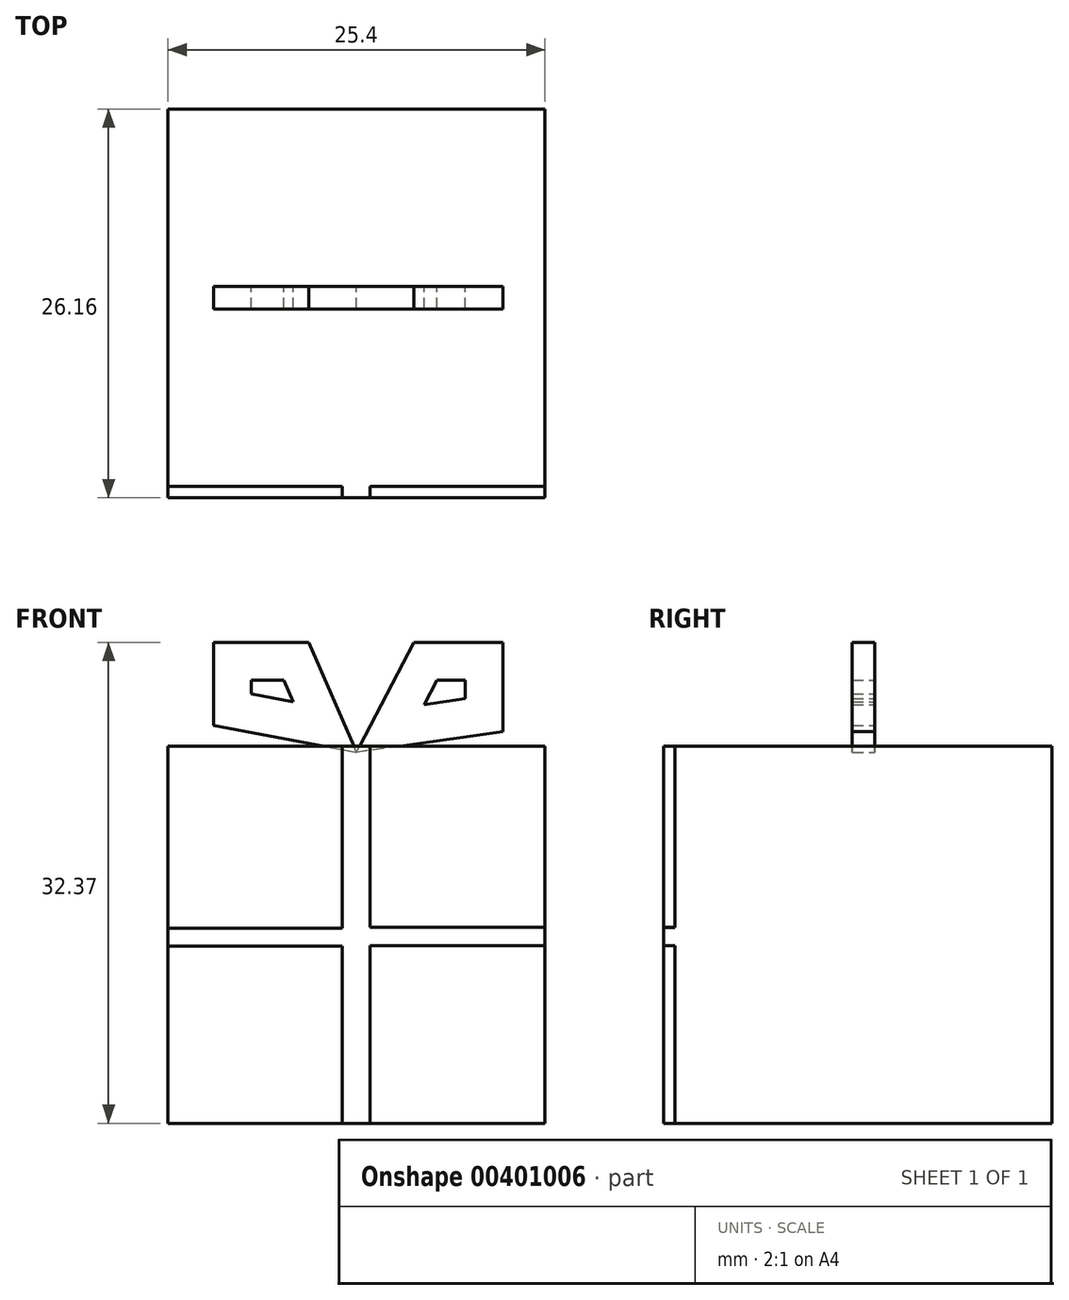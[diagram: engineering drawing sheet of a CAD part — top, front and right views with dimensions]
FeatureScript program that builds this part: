
annotation { "Feature Type Name" : "Feature", "Feature Type Description" : "" }
export const myFeature = defineFeature(function(context is Context, id is Id, definition is map)
    precondition{}
    {
        {
            var Q0;
            Q0=qCreatedBy(makeId("Right.planeOp"),FACE);
            var sketch = newSketch(context, id + "F0", { "sketchPlane" : qUnion([Q0])});
            skLineSegment(sketch, "E0.bottom", {"start": v(12.7, -12.7) * mm, "end": v(-12.7, -12.7) * mm});
            skLineSegment(sketch, "E0.top", {"start": v(12.7, 12.7) * mm, "end": v(-12.7, 12.7) * mm});
            skLineSegment(sketch, "E0.left", {"start": v(12.7, -12.7) * mm, "end": v(12.7, 12.7) * mm});
            skLineSegment(sketch, "E0.right", {"start": v(-12.7, -12.7) * mm, "end": v(-12.7, 12.7) * mm});
            skPoint(sketch, "E0.middle", {"position": v(0, 0) * mm});
            skSolve(sketch);
        }
        {
            var Q0;
            Q0=makeQuery(id+"F0.imprint","IMPRINT",FACE,{"disambiguationData":[TD([[makeQuery(id+"F0.imprint","IMPRINT",EDGE,{"derivedFrom":sQuery(id+"F0.wireOp",EDGE,"E0.bottom")}),-1.0]])]});
            extrude(context, id + "F1", {"entities" : qUnion([Q0]), "endBound" : BoundingType.SYMMETRIC, "oppositeDirection" : true, "depth" : 25.4 * mm});
        }
        {
            var Q0;
            Q0=qCreatedBy(makeId("Front.planeOp"),FACE);
            var sketch = newSketch(context, id + "F2", { "sketchPlane" : qUnion([Q0])});
            skLineSegment(sketch, "E1", {"start": v(0, 14.26) * mm, "end": v(-3.23, 21.65) * mm});
            skLineSegment(sketch, "E2", {"start": v(-3.23, 21.65) * mm, "end": v(-9.64, 21.65) * mm});
            skLineSegment(sketch, "E3", {"start": v(-9.64, 21.65) * mm, "end": v(-9.64, 16.08) * mm});
            skLineSegment(sketch, "E4", {"start": v(-9.64, 16.08) * mm, "end": v(0, 14.26) * mm});
            skLineSegment(sketch, "E5", {"start": v(0, 14.26) * mm, "end": v(3.88, 21.65) * mm});
            skLineSegment(sketch, "E6", {"start": v(3.88, 21.65) * mm, "end": v(9.87, 21.65) * mm});
            skLineSegment(sketch, "E7", {"start": v(9.87, 21.65) * mm, "end": v(9.87, 15.66) * mm});
            skLineSegment(sketch, "E8", {"start": v(9.87, 15.66) * mm, "end": v(0, 14.26) * mm});
            skSolve(sketch);
        }
        {
            var Q0;
            Q0=makeQuery(id+"F2.imprint","IMPRINT",FACE,{"disambiguationData":[TD([[makeQuery(id+"F2.imprint","IMPRINT",EDGE,{"derivedFrom":sQuery(id+"F2.wireOp",EDGE,"E5")}),-1.0]])]});
            var Q1;
            Q1=makeQuery(id+"F2.imprint","IMPRINT",FACE,{"disambiguationData":[TD([[makeQuery(id+"F2.imprint","IMPRINT",EDGE,{"derivedFrom":sQuery(id+"F2.wireOp",EDGE,"E1")}),1.0]])]});
            extrude(context, id + "F3", {"entities" : qUnion([Q0, Q1]), "endBound" : BoundingType.SYMMETRIC, "depth" : 1.52 * mm});
        }
        {
            var Q0;
            Q0=makeQuery(id+"F3.opExtrude","CAP_FACE",FACE,{"disambiguationData":[OSD([sQuery(id+"F2.wireOp",EDGE,"E5"),sQuery(id+"F2.wireOp",EDGE,"E6"),sQuery(id+"F2.wireOp",EDGE,"E7"),sQuery(id+"F2.wireOp",EDGE,"E8")])],"isStart":true});
            var Q1;
            Q1=makeQuery(id+"F3.opExtrude","CAP_FACE",FACE,{"disambiguationData":[OSD([sQuery(id+"F2.wireOp",EDGE,"E5"),sQuery(id+"F2.wireOp",EDGE,"E6"),sQuery(id+"F2.wireOp",EDGE,"E7"),sQuery(id+"F2.wireOp",EDGE,"E8")])],"isStart":false});
            var Q2;
            Q2=makeQuery(id+"F3.opExtrude","CAP_FACE",FACE,{"disambiguationData":[OSD([sQuery(id+"F2.wireOp",EDGE,"E1"),sQuery(id+"F2.wireOp",EDGE,"E2"),sQuery(id+"F2.wireOp",EDGE,"E3"),sQuery(id+"F2.wireOp",EDGE,"E4")])],"isStart":false});
            var Q3;
            Q3=makeQuery(id+"F3.opExtrude","CAP_FACE",FACE,{"disambiguationData":[OSD([sQuery(id+"F2.wireOp",EDGE,"E1"),sQuery(id+"F2.wireOp",EDGE,"E2"),sQuery(id+"F2.wireOp",EDGE,"E3"),sQuery(id+"F2.wireOp",EDGE,"E4")])],"isStart":true});
            var Q4;
            Q4=makeQuery(id+"F3.opExtrude","SWEPT_BODY",BODY,{"disambiguationData":[OSD([sQuery(id+"F2.wireOp",EDGE,"E5"),sQuery(id+"F2.wireOp",EDGE,"E6"),sQuery(id+"F2.wireOp",EDGE,"E7"),sQuery(id+"F2.wireOp",EDGE,"E8")])]});
            var Q5;
            Q5=makeQuery(id+"F3.opExtrude","SWEPT_BODY",BODY,{"disambiguationData":[OSD([sQuery(id+"F2.wireOp",EDGE,"E1"),sQuery(id+"F2.wireOp",EDGE,"E2"),sQuery(id+"F2.wireOp",EDGE,"E3"),sQuery(id+"F2.wireOp",EDGE,"E4")])]});
            shell(context, id + "F4", {"entities" : qUnion([Q0, Q1, Q2, Q3]), "parts" : qUnion([Q4, Q5]), "thickness" : 2.54 * mm});
        }
        {
            var Q0;
            Q0=makeQuery(id+"F3.opExtrude","SWEPT_BODY",BODY,{"disambiguationData":[OSD([sQuery(id+"F2.wireOp",EDGE,"E1"),sQuery(id+"F2.wireOp",EDGE,"E2"),sQuery(id+"F2.wireOp",EDGE,"E3"),sQuery(id+"F2.wireOp",EDGE,"E4")])]});
            var Q1;
            Q1=makeQuery(id+"F3.opExtrude","SWEPT_BODY",BODY,{"disambiguationData":[OSD([sQuery(id+"F2.wireOp",EDGE,"E5"),sQuery(id+"F2.wireOp",EDGE,"E6"),sQuery(id+"F2.wireOp",EDGE,"E7"),sQuery(id+"F2.wireOp",EDGE,"E8")])]});
            transform(context, id + "F5", {"entities" : qUnion([Q0, Q1]), "transformType" : TransformType.TRANSLATION_3D, "dx" : 0 * mm, "dy" : 0 * mm, "dz" : -1.98 * mm, "makeCopy" : false});
        }
        {
            var Q0;
            Q0=makeQuery(id+"F1.opExtrude","SWEPT_FACE",FACE,{"disambiguationData":[OSD([sQuery(id+"F0.wireOp",EDGE,"E0.right")])]});
            var sketch = newSketch(context, id + "F6", { "sketchPlane" : qUnion([Q0])});
            skLineSegment(sketch, "E9", {"start": v(-0.95, 12.7) * mm, "end": v(-0.95, -12.7) * mm});
            skLineSegment(sketch, "E10", {"start": v(-0.95, -12.7) * mm, "end": v(0.92, -12.7) * mm});
            skLineSegment(sketch, "E11", {"start": v(0.92, -12.7) * mm, "end": v(0.92, 12.7) * mm});
            skLineSegment(sketch, "E12", {"start": v(0.92, 12.7) * mm, "end": v(-0.95, 12.7) * mm});
            skSolve(sketch);
        }
        {
            var Q0;
            Q0=makeQuery(id+"F6.imprint","IMPRINT",FACE,{"disambiguationData":[TD([[makeQuery(id+"F6.imprint","IMPRINT",EDGE,{"derivedFrom":sQuery(id+"F6.wireOp",EDGE,"E9")}),1.0]])]});
            extrude(context, id + "F7", {"entities" : qUnion([Q0]), "operationType" : NewBodyOperationType.ADD, "depth" : 0.76 * mm});
        }
        {
            var Q0;
            {var subQ1=sQuery(id+"F0.wireOp",EDGE,"E0.right");Q0=makeQuery(id+"F7.boolean.opBoolean","SPLIT",FACE,{"disambiguationData":[TD([makeQuery(id+"F7.opExtrude","SWEPT_FACE",FACE,{"disambiguationData":[OSD([sQuery(id+"F6.wireOp",EDGE,"E9")])]})])],"derivedFrom":makeQuery(id+"F1.opExtrude","SWEPT_FACE",FACE,{"disambiguationData":[OSD([subQ1])]})});}
            var sketch = newSketch(context, id + "F8", { "sketchPlane" : qUnion([Q0])});
            skLineSegment(sketch, "E13", {"start": v(-12.7, -0.78) * mm, "end": v(-0.95, -0.78) * mm});
            skLineSegment(sketch, "E14", {"start": v(-0.95, -0.78) * mm, "end": v(-0.95, 0.42) * mm});
            skLineSegment(sketch, "E15", {"start": v(-0.95, 0.42) * mm, "end": v(-12.7, 0.42) * mm});
            skLineSegment(sketch, "E16", {"start": v(-12.7, 0.42) * mm, "end": v(-12.7, -0.78) * mm});
            skSolve(sketch);
        }
        {
            var Q0;
            Q0=makeQuery(id+"F8.imprint","IMPRINT",FACE,{"disambiguationData":[TD([[makeQuery(id+"F8.imprint","IMPRINT",EDGE,{"derivedFrom":sQuery(id+"F8.wireOp",EDGE,"E13")}),1.0]])]});
            extrude(context, id + "F9", {"entities" : qUnion([Q0]), "operationType" : NewBodyOperationType.ADD, "depth" : 0.76 * mm});
        }
        {
            var Q0;
            {var subQ1=sQuery(id+"F0.wireOp",EDGE,"E0.right");Q0=makeQuery(id+"F7.boolean.opBoolean","SPLIT",FACE,{"disambiguationData":[TD([makeQuery(id+"F7.opExtrude","SWEPT_FACE",FACE,{"disambiguationData":[OSD([sQuery(id+"F6.wireOp",EDGE,"E11")])]})])],"derivedFrom":makeQuery(id+"F1.opExtrude","SWEPT_FACE",FACE,{"disambiguationData":[OSD([subQ1])]})});}
            var sketch = newSketch(context, id + "F10", { "sketchPlane" : qUnion([Q0])});
            skLineSegment(sketch, "E17", {"start": v(0.92, -0.76) * mm, "end": v(12.7, -0.76) * mm});
            skLineSegment(sketch, "E18", {"start": v(12.7, -0.76) * mm, "end": v(12.7, 0.5) * mm});
            skLineSegment(sketch, "E19", {"start": v(12.7, 0.5) * mm, "end": v(0.92, 0.5) * mm});
            skLineSegment(sketch, "E20", {"start": v(0.92, 0.5) * mm, "end": v(0.92, -0.76) * mm});
            skSolve(sketch);
        }
        {
            var Q0;
            Q0=makeQuery(id+"F10.imprint","IMPRINT",FACE,{"disambiguationData":[TD([[makeQuery(id+"F10.imprint","IMPRINT",EDGE,{"derivedFrom":sQuery(id+"F10.wireOp",EDGE,"E17")}),1.0]])]});
            extrude(context, id + "F11", {"entities" : qUnion([Q0]), "operationType" : NewBodyOperationType.ADD, "depth" : 0.76 * mm});
        }
    });
